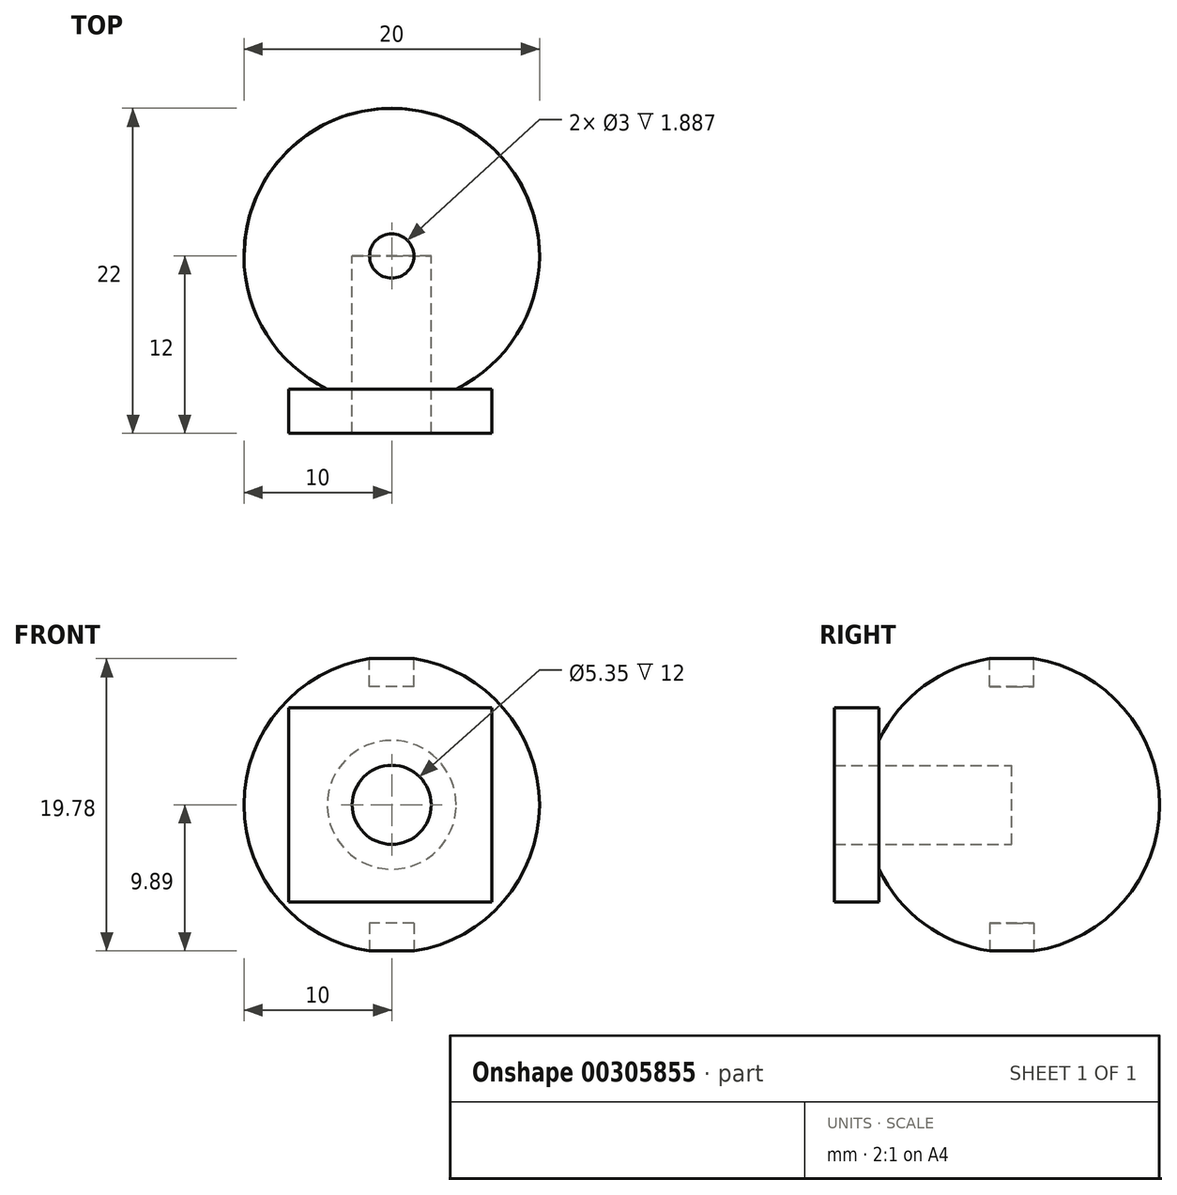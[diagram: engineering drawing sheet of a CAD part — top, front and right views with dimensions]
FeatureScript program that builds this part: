
annotation { "Feature Type Name" : "Feature", "Feature Type Description" : "" }
export const myFeature = defineFeature(function(context is Context, id is Id, definition is map)
    precondition{}
    {
        {
            var Q0;
            Q0=qCreatedBy(makeId("Front.planeOp"),FACE);
            var sketch = newSketch(context, id + "F0", { "sketchPlane" : qUnion([Q0])});
            skPoint(sketch, "E0.endSnap0", {"position": v(0, -12.5) * mm});
            skArc(sketch, "E1", {"start": v(-10, 0) * mm, "mid": v(0, -10) * mm, "end": v(10, 0) * mm});
            skLineSegment(sketch, "E2", {"start": v(-10, 0) * mm, "end": v(10, 0) * mm});
            skSolve(sketch);
        }
        {
            var Q0;
            Q0=makeQuery(id+"F0.imprint","IMPRINT",FACE,{"disambiguationData":[TD([[makeQuery(id+"F0.imprint","IMPRINT",EDGE,{"derivedFrom":sQuery(id+"F0.wireOp",EDGE,"E1")}),1.0]])]});
            var Q1;
            Q1=sQuery(id+"F0.wireOp",EDGE,"E2");
            revolve(context, id + "F1", {"entities" : qUnion([Q0]), "axis" : qUnion([Q1]), "revolveType" : RevolveType.FULL});
        }
        {
            var Q0;
            Q0=qCreatedBy(makeId("Front.planeOp"),FACE);
            var sketch = newSketch(context, id + "F2", { "sketchPlane" : qUnion([Q0])});
            skCircle(sketch, "E3", {"center": v(0, 0) * mm, "radius": 2.67 * mm});
            skSolve(sketch);
        }
        {
            var Q0;
            Q0=qCreatedBy(makeId("Right.planeOp"),FACE);
            cPlane(context, id + "F3", {"entities" : qUnion([Q0]), "cplaneType" : CPlaneType.OFFSET, "offset" : 10 * mm, "width" : 150 * mm, "height" : 150 * mm});
        }
        {
            var Q0;
            Q0=qCreatedBy(makeId("Top.planeOp"),FACE);
            cPlane(context, id + "F4", {"entities" : qUnion([Q0]), "cplaneType" : CPlaneType.OFFSET, "offset" : 10 * mm, "width" : 150 * mm, "height" : 150 * mm});
        }
        {
            var Q0;
            Q0=qCreatedBy(makeId("Top.planeOp"),FACE);
            cPlane(context, id + "F5", {"entities" : qUnion([Q0]), "cplaneType" : CPlaneType.OFFSET, "offset" : 10 * mm, "oppositeDirection" : true, "width" : 150 * mm, "height" : 150 * mm});
        }
        {
            var Q0;
            Q0=qCreatedBy(makeId("Right.planeOp"),FACE);
            cPlane(context, id + "F6", {"entities" : qUnion([Q0]), "cplaneType" : CPlaneType.OFFSET, "offset" : 10 * mm, "oppositeDirection" : true, "width" : 150 * mm, "height" : 150 * mm});
        }
        {
            var Q0;
            Q0=qCreatedBy(id+"F4.planeOp",FACE);
            var sketch = newSketch(context, id + "F7", { "sketchPlane" : qUnion([Q0])});
            skCircle(sketch, "E4", {"center": v(0, 0) * mm, "radius": 1.5 * mm});
            skSolve(sketch);
        }
        {
            var Q0;
            Q0=qCreatedBy(id+"F5.planeOp",FACE);
            var sketch = newSketch(context, id + "F8", { "sketchPlane" : qUnion([Q0])});
            skCircle(sketch, "E5", {"center": v(0, 0) * mm, "radius": 1.5 * mm});
            skSolve(sketch);
        }
        {
            var Q0;
            Q0=qSketchRegion(id+"F7",true);
            extrude(context, id + "F9", {"entities" : qUnion([Q0]), "operationType" : NewBodyOperationType.REMOVE, "oppositeDirection" : true, "depth" : 2 * mm});
        }
        {
            var Q0;
            Q0=qSketchRegion(id+"F8",true);
            extrude(context, id + "F10", {"entities" : qUnion([Q0]), "operationType" : NewBodyOperationType.REMOVE, "depth" : 2 * mm});
        }
        {
            var Q0;
            Q0=qCreatedBy(makeId("Front.planeOp"),FACE);
            cPlane(context, id + "F11", {"entities" : qUnion([Q0]), "cplaneType" : CPlaneType.OFFSET, "offset" : 9 * mm, "width" : 150 * mm, "height" : 150 * mm});
        }
        {
            var Q0;
            Q0=qCreatedBy(id+"F11.planeOp",FACE);
            var sketch = newSketch(context, id + "F12", { "sketchPlane" : qUnion([Q0])});
            skLineSegment(sketch, "E6.bottom", {"start": v(6.78, 6.58) * mm, "end": v(-6.96, 6.58) * mm});
            skLineSegment(sketch, "E6.top", {"start": v(6.78, -6.58) * mm, "end": v(-6.96, -6.58) * mm});
            skLineSegment(sketch, "E6.left", {"start": v(6.78, 6.58) * mm, "end": v(6.78, -6.58) * mm});
            skLineSegment(sketch, "E6.right", {"start": v(-6.96, 6.58) * mm, "end": v(-6.96, -6.58) * mm});
            skSolve(sketch);
        }
        {
            var Q0;
            Q0=qSketchRegion(id+"F12",true);
            extrude(context, id + "F13", {"entities" : qUnion([Q0]), "operationType" : NewBodyOperationType.ADD, "depth" : 3 * mm});
        }
        {
            var Q0;
            Q0=qSketchRegion(id+"F2",true);
            var Q1;
            Q1=sQuery(id+"F2.wireOp",EDGE,"E3");
            extrude(context, id + "F14", {"entities" : qUnion([Q0]), "operationType" : NewBodyOperationType.REMOVE, "surfaceEntities" : qUnion([Q1]), "endBound" : BoundingType.THROUGH_ALL, "depth" : 50 * mm});
        }
    });
